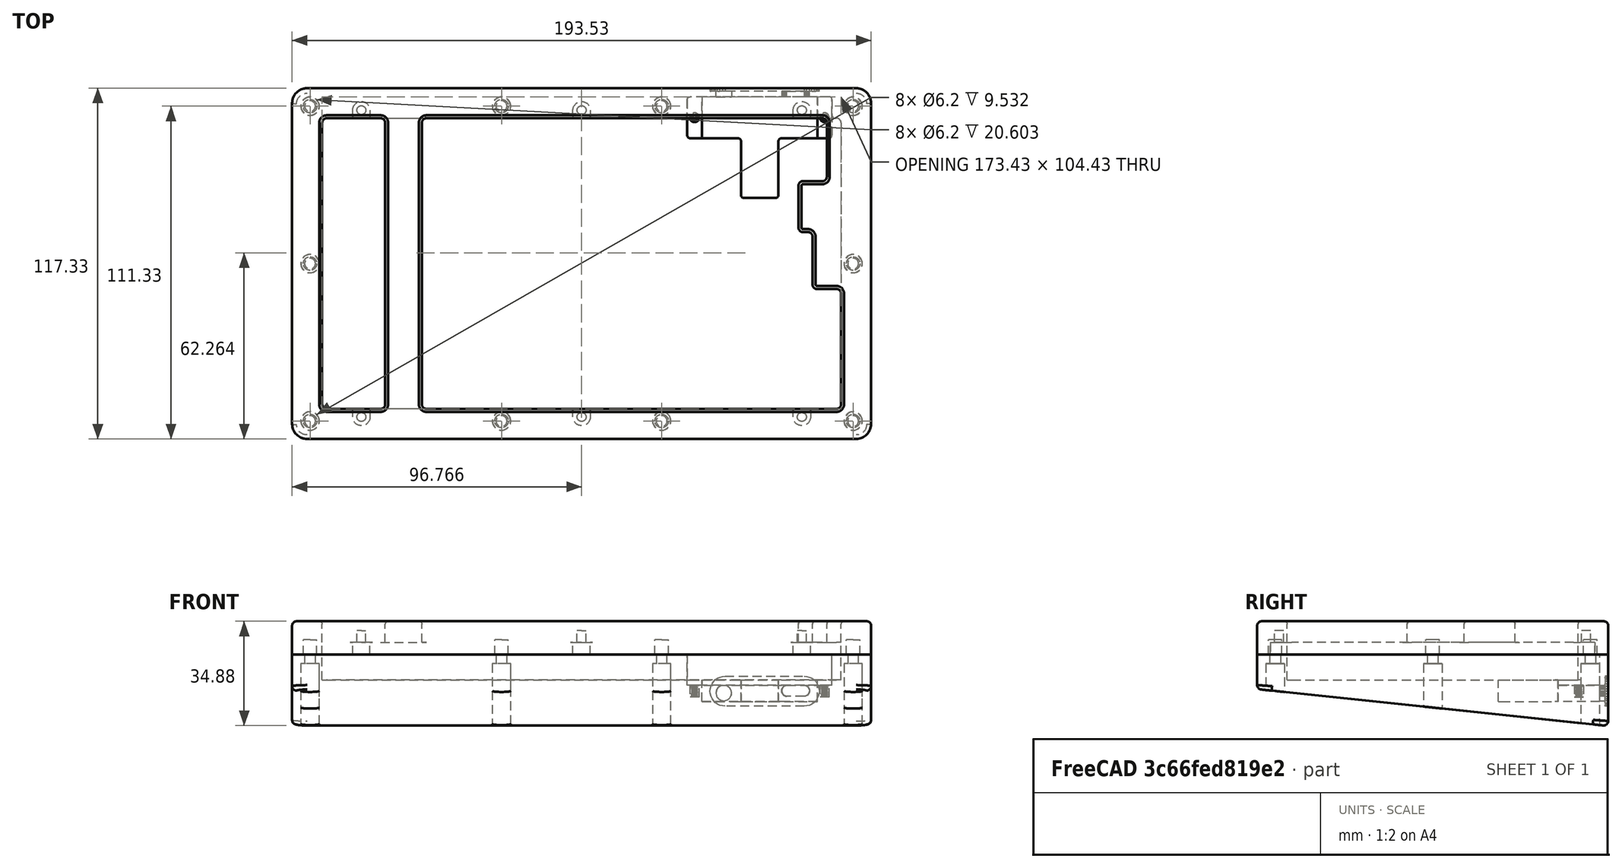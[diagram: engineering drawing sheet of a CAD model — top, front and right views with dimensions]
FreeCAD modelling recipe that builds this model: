
FCSTD DOCUMENT  (FreeCAD 0.21R33771 (Git))
Label: case_left
License: All rights reserved
LicenseURL: https://en.wikipedia.org/wiki/All_rights_reserved
objects: Part::Cylinder×44, Part::MultiFuse×41, Part::Feature×31, Part::Cut×19, Part::Fillet×18, Part::Extrusion×10, Part::Box×7, Part::FeaturePython×2
note: 172 computed .brp shape members not serialized (recipe doc carries the construction recipe); baked Part::Feature solids carry a one-line shape summary decoded from their .brp

FEATURE [Part::Feature] rect40_3 .. rect40_012  x10 (patterned run collapsed; names and placements below)
  shape: bbox 4.5 x 4.5 x 2e-07 mm, 0 faces, 0 solids (baked)
FEATURE [Part::Feature] rect40_013
  shape: bbox 173.4 x 108.4 x 2e-07 mm, 0 faces, 0 solids (baked)
FEATURE [Part::Box] Box  label="立方体"
  AttacherType = Attacher::AttachEngine3D
  Height = 11.2
  Length = 193.53
  Placement = pos=(0,-117.33,0) rot=(0,0,1;0rad)
  Width = 117.33
FEATURE [Part::MultiFuse] Fusion
  Shapes = -> [rect40_012,rect40_004,rect40_005,rect40_006,rect40_007,rect40_008,rect40_009,rect40_010,rect40_011,rect40_3]
FEATURE [Part::Extrusion] Extrude
  Base = -> Fusion
  Dir = (0,0,1)
  DirMode = 0
  FaceMakerClass = Part::FaceMakerBullseye
  LengthFwd = 5
  LengthRev = 0
  Solid = true
  Symmetric = false
FEATURE [Part::Extrusion] Extrude001
  Base = -> rect40_013
  Dir = (0,0,1)
  DirMode = 0
  FaceMakerClass = Part::FaceMakerBullseye
  LengthFwd = 4.1
  LengthRev = 0
  Solid = true
  Symmetric = false
FEATURE [Part::Cut] Cut
  Base = -> Box
  Tool = -> Extrude
FEATURE [Part::Cut] Cut001
  Base = -> Cut
  Tool = -> Extrude001
FEATURE [Part::Box] Box001  label="立方体001"
  AttacherType = Attacher::AttachEngine3D
  Height = 30
  Length = 193.53
  Placement = pos=(0,-117.33,-20) rot=(0,0,1;0rad)
  Width = 117.33
FEATURE [Part::Feature] path6845_6_2_7_83 .. path6845_6_2_7_088  x6 (patterned run collapsed; names and placements below)
  shape: bbox 3 x 3 x 2e-07 mm, 0 faces, 0 solids (baked)
FEATURE [Part::MultiFuse] Fusion001
  Shapes = -> [path6845_6_2_7_088,path6845_6_2_7_83,path6845_6_2_7_084,path6845_6_2_7_085,path6845_6_2_7_086,path6845_6_2_7_087]
FEATURE [Part::Extrusion] Extrude002
  Base = -> Fusion001
  Dir = (0,0,1)
  DirMode = 0
  FaceMakerClass = Part::FaceMakerBullseye
  LengthFwd = 4
  LengthRev = 0
  Placement = pos=(0,0,4.1) rot=(0,0,1;0rad)
  Solid = true
  Symmetric = false
FEATURE [Part::Cut] Cut002
  Base = -> Cut001
  Tool = -> Extrude002
FEATURE [Part::Feature] path44_5_0
  shape: bbox 140.1 x 97.23 x 2e-07 mm, 0 faces, 0 solids (baked)
FEATURE [Part::Feature] path44_5_001
  shape: bbox 21.05 x 97.23 x 2e-07 mm, 0 faces, 0 solids (baked)
FEATURE [Part::MultiFuse] Fusion002
  Shapes = -> [path44_5_0,path44_5_001]
FEATURE [Part::Extrusion] Extrude003
  Base = -> Fusion002
  Dir = (0,0,1)
  DirMode = 0
  FaceMakerClass = Part::FaceMakerBullseye
  LengthFwd = 7.1
  LengthRev = 0
  Placement = pos=(0,0,4.1) rot=(0,0,1;0rad)
  Solid = true
  Symmetric = false
FEATURE [Part::Fillet] Fillet
  Base = -> Cut002
  Edges = 12 edges r=0.8: [Edge135,Edge144,Edge146,Edge154,Edge156,Edge164,Edge170,Edge178,Edge180,Edge188,Edge190,Edge198]
FEATURE [Part::Fillet] Fillet001
  Base = -> Fillet
  Edges = 4 edges r=1.5: [Edge93,Edge97,Edge174,Edge178]
FEATURE [Part::Fillet] Fillet002
  Base = -> Extrude003
  Edges = 14 edges r=1.5: [Edge1,Edge2,Edge5,Edge8,Edge11,Edge14,Edge17,Edge20,Edge23,Edge26,Edge31,Edge32,Edge35,Edge38]
FEATURE [Part::Fillet] Fillet003
  Base = -> Fillet001
  Edges = 4 edges r=5: [Edge195,Edge197,Edge198,Edge201]
FEATURE [Part::Cut] Cut003
  Base = -> Fillet003
  Tool = -> Fillet002
FEATURE [Part::Box] Box002  label="立方体002"
  AttacherType = Attacher::AttachEngine3D
  Height = 100
  Length = 193.53
  Placement = pos=(0,-129.33,-100.8) rot=(-1,0,0;0.10472rad)
  Width = 150
FEATURE [Part::Cut] Cut004
  Base = -> Box001
  Tool = -> Box002
FEATURE [Part::Fillet] Fillet005
  Base = -> Cut004
  Edges = 4 edges r=5: [Edge1,Edge3,Edge5,Edge10]
FEATURE [Part::Fillet] Fillet006
  Base = -> Fillet005
  Edges = 8 edges r=1.5: [Edge3,Edge12,Edge14,Edge16,Edge17,Edge18,Edge19,Edge20]
FEATURE [Part::Fillet] Fillet007
  Base = -> Cut003
  Edges = 8 edges r=1.5: [Edge99,Edge103,Edge104,Edge107,Edge108,Edge111,Edge113,Edge114]
FEATURE [Part::Fillet] Fillet008  label="top_left"
  Base = -> Fillet007
  Edges = 28 edges r=1: [Edge119,Edge120,Edge121,Edge122,Edge123,Edge124,Edge125,Edge126,Edge127,Edge128,Edge129,Edge130,Edge131,Edge132,Edge133,Edge134,Edge135,Edge136,Edge137,Edge138,Edge139,Edge140,Edge141,Edge142,Edge143,Edge144,Edge145,Edge146]
  Placement = pos=(0,0,10) rot=(0,0,1;0rad)
FEATURE [Part::Cylinder] Cylinder045  label="円柱045"
  Angle = 360
  AttacherType = Attacher::AttachEngine3D
  FirstAngle = 0
  Height = 30
  Placement = pos=(0,0,-32) rot=(0,0,1;0rad)
  Radius = 3.1
  SecondAngle = 0
FEATURE [Part::Cylinder] Cylinder046  label="円柱046"
  Angle = 360
  AttacherType = Attacher::AttachEngine3D
  FirstAngle = 0
  Height = 20
  Placement = pos=(0,0,-10) rot=(0,0,1;0rad)
  Radius = 1.8
  SecondAngle = 0
FEATURE [Part::MultiFuse] Fusion048
  Placement = pos=(6,-6,0) rot=(0,0,1;0rad)
  Shapes = -> [Cylinder046,Cylinder045]
FEATURE [Part::Cylinder] Cylinder047  label="円柱047"
  Angle = 360
  AttacherType = Attacher::AttachEngine3D
  FirstAngle = 0
  Height = 30
  Placement = pos=(0,0,-32) rot=(0,0,1;0rad)
  Radius = 3.1
  SecondAngle = 0
FEATURE [Part::Cylinder] Cylinder048  label="円柱048"
  Angle = 360
  AttacherType = Attacher::AttachEngine3D
  FirstAngle = 0
  Height = 20
  Placement = pos=(0,0,-10) rot=(0,0,1;0rad)
  Radius = 1.8
  SecondAngle = 0
FEATURE [Part::MultiFuse] Fusion049
  Placement = pos=(6,-58.67,0) rot=(0,0,1;0rad)
  Shapes = -> [Cylinder048,Cylinder047]
FEATURE [Part::Cylinder] Cylinder049  label="円柱049"
  Angle = 360
  AttacherType = Attacher::AttachEngine3D
  FirstAngle = 0
  Height = 30
  Placement = pos=(0,0,-32) rot=(0,0,1;0rad)
  Radius = 3.1
  SecondAngle = 0
FEATURE [Part::Cylinder] Cylinder050  label="円柱050"
  Angle = 360
  AttacherType = Attacher::AttachEngine3D
  FirstAngle = 0
  Height = 20
  Placement = pos=(0,0,-10) rot=(0,0,1;0rad)
  Radius = 1.8
  SecondAngle = 0
FEATURE [Part::MultiFuse] Fusion050
  Placement = pos=(6,-111.34,0) rot=(0,0,1;0rad)
  Shapes = -> [Cylinder050,Cylinder049]
FEATURE [Part::MultiFuse] Fusion051
  Shapes = -> [Fusion050,Fusion049,Fusion048]
FEATURE [Part::Cylinder] Cylinder051  label="円柱051"
  Angle = 360
  AttacherType = Attacher::AttachEngine3D
  FirstAngle = 0
  Height = 30
  Placement = pos=(0,0,-32) rot=(0,0,1;0rad)
  Radius = 3.1
  SecondAngle = 0
FEATURE [Part::Cylinder] Cylinder052  label="円柱052"
  Angle = 360
  AttacherType = Attacher::AttachEngine3D
  FirstAngle = 0
  Height = 20
  Placement = pos=(0,0,-10) rot=(0,0,1;0rad)
  Radius = 1.8
  SecondAngle = 0
FEATURE [Part::Cylinder] Cylinder055  label="円柱055"
  Angle = 360
  AttacherType = Attacher::AttachEngine3D
  FirstAngle = 0
  Height = 30
  Placement = pos=(0,0,-32) rot=(0,0,1;0rad)
  Radius = 3.1
  SecondAngle = 0
FEATURE [Part::Cylinder] Cylinder056  label="円柱056"
  Angle = 360
  AttacherType = Attacher::AttachEngine3D
  FirstAngle = 0
  Height = 20
  Placement = pos=(0,0,-10) rot=(0,0,1;0rad)
  Radius = 1.8
  SecondAngle = 0
FEATURE [Part::MultiFuse] Fusion052
  Placement = pos=(6,-6,0) rot=(0,0,1;0rad)
  Shapes = -> [Cylinder052,Cylinder051]
FEATURE [Part::MultiFuse] Fusion054
  Placement = pos=(6,-111.34,0) rot=(0,0,1;0rad)
  Shapes = -> [Cylinder056,Cylinder055]
FEATURE [Part::MultiFuse] Fusion055
  Placement = pos=(64,0,0) rot=(0,0,1;0rad)
  Shapes = -> [Fusion054,Fusion052]
FEATURE [Part::Cylinder] Cylinder057  label="円柱057"
  Angle = 360
  AttacherType = Attacher::AttachEngine3D
  FirstAngle = 0
  Height = 30
  Placement = pos=(0,0,-32) rot=(0,0,1;0rad)
  Radius = 3.1
  SecondAngle = 0
FEATURE [Part::Cylinder] Cylinder058  label="円柱058"
  Angle = 360
  AttacherType = Attacher::AttachEngine3D
  FirstAngle = 0
  Height = 20
  Placement = pos=(0,0,-10) rot=(0,0,1;0rad)
  Radius = 1.8
  SecondAngle = 0
FEATURE [Part::Cylinder] Cylinder061  label="円柱061"
  Angle = 360
  AttacherType = Attacher::AttachEngine3D
  FirstAngle = 0
  Height = 30
  Placement = pos=(0,0,-32) rot=(0,0,1;0rad)
  Radius = 3.1
  SecondAngle = 0
FEATURE [Part::Cylinder] Cylinder062  label="円柱062"
  Angle = 360
  AttacherType = Attacher::AttachEngine3D
  FirstAngle = 0
  Height = 20
  Placement = pos=(0,0,-10) rot=(0,0,1;0rad)
  Radius = 1.8
  SecondAngle = 0
FEATURE [Part::MultiFuse] Fusion056
  Placement = pos=(6,-6,0) rot=(0,0,1;0rad)
  Shapes = -> [Cylinder058,Cylinder057]
FEATURE [Part::MultiFuse] Fusion058
  Placement = pos=(6,-111.34,0) rot=(0,0,1;0rad)
  Shapes = -> [Cylinder062,Cylinder061]
FEATURE [Part::MultiFuse] Fusion059
  Placement = pos=(117.53,0,0) rot=(0,0,1;0rad)
  Shapes = -> [Fusion058,Fusion056]
FEATURE [Part::Cylinder] Cylinder063  label="円柱063"
  Angle = 360
  AttacherType = Attacher::AttachEngine3D
  FirstAngle = 0
  Height = 30
  Placement = pos=(0,0,-32) rot=(0,0,1;0rad)
  Radius = 3.1
  SecondAngle = 0
FEATURE [Part::Cylinder] Cylinder064  label="円柱064"
  Angle = 360
  AttacherType = Attacher::AttachEngine3D
  FirstAngle = 0
  Height = 20
  Placement = pos=(0,0,-10) rot=(0,0,1;0rad)
  Radius = 1.8
  SecondAngle = 0
FEATURE [Part::Cylinder] Cylinder065  label="円柱065"
  Angle = 360
  AttacherType = Attacher::AttachEngine3D
  FirstAngle = 0
  Height = 30
  Placement = pos=(0,0,-32) rot=(0,0,1;0rad)
  Radius = 3.1
  SecondAngle = 0
FEATURE [Part::Cylinder] Cylinder066  label="円柱066"
  Angle = 360
  AttacherType = Attacher::AttachEngine3D
  FirstAngle = 0
  Height = 20
  Placement = pos=(0,0,-10) rot=(0,0,1;0rad)
  Radius = 1.8
  SecondAngle = 0
FEATURE [Part::Cylinder] Cylinder067  label="円柱067"
  Angle = 360
  AttacherType = Attacher::AttachEngine3D
  FirstAngle = 0
  Height = 30
  Placement = pos=(0,0,-32) rot=(0,0,1;0rad)
  Radius = 3.1
  SecondAngle = 0
FEATURE [Part::Cylinder] Cylinder068  label="円柱068"
  Angle = 360
  AttacherType = Attacher::AttachEngine3D
  FirstAngle = 0
  Height = 20
  Placement = pos=(0,0,-10) rot=(0,0,1;0rad)
  Radius = 1.8
  SecondAngle = 0
FEATURE [Part::MultiFuse] Fusion060
  Placement = pos=(6,-6,0) rot=(0,0,1;0rad)
  Shapes = -> [Cylinder064,Cylinder063]
FEATURE [Part::MultiFuse] Fusion061
  Placement = pos=(6,-58.67,0) rot=(0,0,1;0rad)
  Shapes = -> [Cylinder066,Cylinder065]
FEATURE [Part::MultiFuse] Fusion062
  Placement = pos=(6,-111.34,0) rot=(0,0,1;0rad)
  Shapes = -> [Cylinder068,Cylinder067]
FEATURE [Part::MultiFuse] Fusion063
  Placement = pos=(181.53,0,0) rot=(0,0,1;0rad)
  Shapes = -> [Fusion062,Fusion061,Fusion060]
FEATURE [Part::MultiFuse] Fusion064
  Placement = pos=(0,0,9) rot=(0,0,1;0rad)
  Shapes = -> [Fusion063,Fusion059,Fusion055,Fusion051]
FEATURE [Part::Cut] Cut005
  Base = -> Fillet006
  Tool = -> Fusion064
FEATURE [Part::Feature] path6845_6_2_7_83_9
  shape: bbox 173.4 x 97.23 x 2e-07 mm, 0 faces, 0 solids (baked)
FEATURE [Part::Extrusion] Extrude004
  Base = -> path6845_6_2_7_83_9
  Dir = (0,0,1)
  DirMode = 0
  FaceMakerClass = Part::FaceMakerBullseye
  LengthFwd = 8.5
  LengthRev = 0
  Placement = pos=(0,0,1.5) rot=(0,0,1;0rad)
  Solid = true
  Symmetric = false
FEATURE [Part::Fillet] Fillet009
  Base = -> Extrude004
  Edges = 4 edges r=1.5: [Edge1,Edge2,Edge5,Edge8]
FEATURE [Part::Cut] Cut006
  Base = -> Cut005
  Tool = -> Fillet009
FEATURE [Part::Cylinder] Cylinder  label="円柱"
  Angle = 360
  AttacherType = Attacher::AttachEngine3D
  FirstAngle = 0
  Height = 4
  Placement = pos=(15.57,-9.8,-4.2) rot=(0,0,1;0rad)
  Radius = 1.55
  SecondAngle = 0
FEATURE [Part::Cylinder] Cylinder069  label="円柱069"
  Angle = 360
  AttacherType = Attacher::AttachEngine3D
  FirstAngle = 0
  Height = 4
  Placement = pos=(59.03,-9.8,-4.2) rot=(0,0,1;0rad)
  Radius = 1.55
  SecondAngle = 0
FEATURE [Part::Cylinder] Cylinder070  label="trrs"
  Angle = 360
  AttacherType = Attacher::AttachEngine3D
  FirstAngle = 0
  Height = 10
  Placement = pos=(144.28,5,-2.81) rot=(1,0,0;1.5708rad)
  Radius = 2.6
  SecondAngle = 0
FEATURE [Part::MultiFuse] Fusion065
  Placement = pos=(118.94,0,0) rot=(0,0,1;0rad)
  Shapes = -> [Cylinder,Cylinder069]
FEATURE [Part::Feature] hull006
  Placement = pos=(0,4.8,0) rot=(0,0,1;0rad)
  shape: bbox 13.02 x 10 x 7.518 mm, 128 faces (baked)
FEATURE [Part::Feature] hull007
  shape: bbox 9.26 x 10 x 3.733 mm, 28 faces (baked)
FEATURE [Part::MultiFuse] Fusion067  label="usb-hole001"
  Placement = pos=(-147.56,-1.85,-4.55) rot=(0,0,1;0rad)
  Shapes = -> [hull006,hull007]
FEATURE [Part::Box] Box003  label="立方体003"
  AttacherType = Attacher::AttachEngine3D
  Height = 7.2
  Length = 12.5
  Placement = pos=(31.05,-36.75,-5.7) rot=(0,0,1;0rad)
  Width = 20
FEATURE [Part::Feature] rect3_6_21_5
  Placement = pos=(0,0,-0.2) rot=(0,0,1;0rad)
  shape: bbox 38.6 x 13.9 x 2e-07 mm, 0 faces, 0 solids (baked)
FEATURE [Part::Extrusion] Extrude007
  Base = -> rect3_6_21_5
  Dir = (0,0,1)
  DirMode = 0
  FaceMakerClass = Part::FaceMakerBullseye
  LengthFwd = 22.2
  LengthRev = 0
  Placement = pos=(0,0,-5.5) rot=(0,0,1;0rad)
  Solid = true
  Symmetric = false
FEATURE [Part::MultiFuse] Fusion066
  Placement = pos=(119,0,0) rot=(0,0,1;0rad)
  Shapes = -> [Extrude007,Box003]
FEATURE [Part::Cut] Cut007
  Base = -> Cut006
  Tool = -> Fusion066
FEATURE [Part::Fillet] Fillet010
  Base = -> Cut007
  Edges = 4 edges r=1: [Edge151,Edge152,Edge154,Edge156]
FEATURE [Part::Feature] rect3_6
  Placement = pos=(0,0,-0.2) rot=(0,0,1;0rad)
  shape: bbox 48.4 x 13.9 x 2e-07 mm, 0 faces, 0 solids (baked)
FEATURE [Part::Extrusion] Extrude008
  Base = -> rect3_6
  Dir = (0,0,1)
  DirMode = 0
  FaceMakerClass = Part::FaceMakerBullseye
  LengthFwd = 16.7
  LengthRev = 0
  Solid = true
  Symmetric = false
FEATURE [Part::Fillet] Fillet011
  Base = -> Extrude008
  Edges = 4 edges r=1: [Edge1,Edge2,Edge5,Edge8]
FEATURE [Part::Cut] Cut008
  Base = -> Fillet010
  Tool = -> Fillet011
FEATURE [Part::Fillet] Fillet012
  Base = -> Cut008
  Edges = 2 edges r=1: [Edge53,Edge72]
FEATURE [Part::Cut] Cut009
  Base = -> Fillet012
  Tool = -> Fusion065
FEATURE [Part::Cut] Cut010
  Base = -> Cut009
  Tool = -> Fusion067
FEATURE [Part::Cut] Cut011
  Base = -> Cut010
  Tool = -> Cylinder070
FEATURE [Part::Feature] hull
  Placement = pos=(121.9,0,0) rot=(0,0,1;0rad)
  shape: bbox 36.5 x 3 x 10 mm, 40 faces (baked)
FEATURE [Part::Cut] Cut012  label="bottom_left"
  Base = -> Cut011
  Tool = -> hull
FEATURE [Part::Box] Box004  label="立方体004"
  AttacherType = Attacher::AttachEngine3D
  Height = 30
  Length = 193.53
  Placement = pos=(0,-117.33,-20) rot=(0,0,1;0rad)
  Width = 117.33
FEATURE [Part::Box] Box005  label="立方体005"
  AttacherType = Attacher::AttachEngine3D
  Height = 100
  Length = 193.53
  Placement = pos=(0,-129.33,-100.8) rot=(-1,0,0;0.10472rad)
  Width = 150
FEATURE [Part::Box] Box006  label="立方体006"
  AttacherType = Attacher::AttachEngine3D
  Height = 7.2
  Length = 12.5
  Placement = pos=(31.05,-36.75,-5.7) rot=(0,0,1;0rad)
  Width = 20
FEATURE [Part::Cut] Cut013
  Base = -> Box004
  Tool = -> Box005
FEATURE [Part::Cylinder] Cylinder072  label="円柱071"
  Angle = 360
  AttacherType = Attacher::AttachEngine3D
  FirstAngle = 0
  Height = 30
  Placement = pos=(0,0,-32) rot=(0,0,1;0rad)
  Radius = 3.1
  SecondAngle = 0
FEATURE [Part::Cylinder] Cylinder073  label="円柱072"
  Angle = 360
  AttacherType = Attacher::AttachEngine3D
  FirstAngle = 0
  Height = 20
  Placement = pos=(0,0,-10) rot=(0,0,1;0rad)
  Radius = 1.8
  SecondAngle = 0
FEATURE [Part::Cylinder] Cylinder074  label="円柱073"
  Angle = 360
  AttacherType = Attacher::AttachEngine3D
  FirstAngle = 0
  Height = 30
  Placement = pos=(0,0,-32) rot=(0,0,1;0rad)
  Radius = 3.1
  SecondAngle = 0
FEATURE [Part::Cylinder] Cylinder075  label="円柱074"
  Angle = 360
  AttacherType = Attacher::AttachEngine3D
  FirstAngle = 0
  Height = 20
  Placement = pos=(0,0,-10) rot=(0,0,1;0rad)
  Radius = 1.8
  SecondAngle = 0
FEATURE [Part::Cylinder] Cylinder076  label="円柱075"
  Angle = 360
  AttacherType = Attacher::AttachEngine3D
  FirstAngle = 0
  Height = 30
  Placement = pos=(0,0,-32) rot=(0,0,1;0rad)
  Radius = 3.1
  SecondAngle = 0
FEATURE [Part::Cylinder] Cylinder077  label="円柱076"
  Angle = 360
  AttacherType = Attacher::AttachEngine3D
  FirstAngle = 0
  Height = 20
  Placement = pos=(0,0,-10) rot=(0,0,1;0rad)
  Radius = 1.8
  SecondAngle = 0
FEATURE [Part::Cylinder] Cylinder078  label="円柱077"
  Angle = 360
  AttacherType = Attacher::AttachEngine3D
  FirstAngle = 0
  Height = 30
  Placement = pos=(0,0,-32) rot=(0,0,1;0rad)
  Radius = 3.1
  SecondAngle = 0
FEATURE [Part::Cylinder] Cylinder079  label="円柱078"
  Angle = 360
  AttacherType = Attacher::AttachEngine3D
  FirstAngle = 0
  Height = 20
  Placement = pos=(0,0,-10) rot=(0,0,1;0rad)
  Radius = 1.8
  SecondAngle = 0
FEATURE [Part::Cylinder] Cylinder080  label="円柱079"
  Angle = 360
  AttacherType = Attacher::AttachEngine3D
  FirstAngle = 0
  Height = 30
  Placement = pos=(0,0,-32) rot=(0,0,1;0rad)
  Radius = 3.1
  SecondAngle = 0
FEATURE [Part::Cylinder] Cylinder081  label="円柱080"
  Angle = 360
  AttacherType = Attacher::AttachEngine3D
  FirstAngle = 0
  Height = 20
  Placement = pos=(0,0,-10) rot=(0,0,1;0rad)
  Radius = 1.8
  SecondAngle = 0
FEATURE [Part::Cylinder] Cylinder082  label="円柱081"
  Angle = 360
  AttacherType = Attacher::AttachEngine3D
  FirstAngle = 0
  Height = 30
  Placement = pos=(0,0,-32) rot=(0,0,1;0rad)
  Radius = 3.1
  SecondAngle = 0
FEATURE [Part::Cylinder] Cylinder083  label="円柱082"
  Angle = 360
  AttacherType = Attacher::AttachEngine3D
  FirstAngle = 0
  Height = 20
  Placement = pos=(0,0,-10) rot=(0,0,1;0rad)
  Radius = 1.8
  SecondAngle = 0
FEATURE [Part::Cylinder] Cylinder084  label="円柱083"
  Angle = 360
  AttacherType = Attacher::AttachEngine3D
  FirstAngle = 0
  Height = 30
  Placement = pos=(0,0,-32) rot=(0,0,1;0rad)
  Radius = 3.1
  SecondAngle = 0
FEATURE [Part::Cylinder] Cylinder085  label="円柱084"
  Angle = 360
  AttacherType = Attacher::AttachEngine3D
  FirstAngle = 0
  Height = 20
  Placement = pos=(0,0,-10) rot=(0,0,1;0rad)
  Radius = 1.8
  SecondAngle = 0
FEATURE [Part::Cylinder] Cylinder086  label="円柱085"
  Angle = 360
  AttacherType = Attacher::AttachEngine3D
  FirstAngle = 0
  Height = 30
  Placement = pos=(0,0,-32) rot=(0,0,1;0rad)
  Radius = 3.1
  SecondAngle = 0
FEATURE [Part::Cylinder] Cylinder087  label="円柱086"
  Angle = 360
  AttacherType = Attacher::AttachEngine3D
  FirstAngle = 0
  Height = 20
  Placement = pos=(0,0,-10) rot=(0,0,1;0rad)
  Radius = 1.8
  SecondAngle = 0
FEATURE [Part::Cylinder] Cylinder088  label="円柱087"
  Angle = 360
  AttacherType = Attacher::AttachEngine3D
  FirstAngle = 0
  Height = 30
  Placement = pos=(0,0,-32) rot=(0,0,1;0rad)
  Radius = 3.1
  SecondAngle = 0
FEATURE [Part::Cylinder] Cylinder089  label="円柱088"
  Angle = 360
  AttacherType = Attacher::AttachEngine3D
  FirstAngle = 0
  Height = 20
  Placement = pos=(0,0,-10) rot=(0,0,1;0rad)
  Radius = 1.8
  SecondAngle = 0
FEATURE [Part::Cylinder] Cylinder090  label="円柱089"
  Angle = 360
  AttacherType = Attacher::AttachEngine3D
  FirstAngle = 0
  Height = 30
  Placement = pos=(0,0,-32) rot=(0,0,1;0rad)
  Radius = 3.1
  SecondAngle = 0
FEATURE [Part::Cylinder] Cylinder091  label="円柱090"
  Angle = 360
  AttacherType = Attacher::AttachEngine3D
  FirstAngle = 0
  Height = 20
  Placement = pos=(0,0,-10) rot=(0,0,1;0rad)
  Radius = 1.8
  SecondAngle = 0
FEATURE [Part::Cylinder] Cylinder093  label="trrs001"
  Angle = 360
  AttacherType = Attacher::AttachEngine3D
  FirstAngle = 0
  Height = 10
  Placement = pos=(144.28,5,-2.81) rot=(1,0,0;1.5708rad)
  Radius = 2.6
  SecondAngle = 0
FEATURE [Part::Fillet] Fillet013
  Base = -> Cut013
  Edges = 4 edges r=5: [Edge1,Edge3,Edge5,Edge10]
FEATURE [Part::Fillet] Fillet014
  Base = -> Fillet013
  Edges = 8 edges r=1.5: [Edge3,Edge12,Edge14,Edge16,Edge17,Edge18,Edge19,Edge20]
FEATURE [Part::MultiFuse] Fusion068
  Placement = pos=(6,-6,0) rot=(0,0,1;0rad)
  Shapes = -> [Cylinder073,Cylinder072]
FEATURE [Part::MultiFuse] Fusion069
  Placement = pos=(6,-58.67,0) rot=(0,0,1;0rad)
  Shapes = -> [Cylinder075,Cylinder074]
FEATURE [Part::MultiFuse] Fusion070
  Placement = pos=(6,-111.34,0) rot=(0,0,1;0rad)
  Shapes = -> [Cylinder077,Cylinder076]
FEATURE [Part::MultiFuse] Fusion071
  Shapes = -> [Fusion070,Fusion069,Fusion068]
FEATURE [Part::MultiFuse] Fusion072
  Placement = pos=(6,-6,0) rot=(0,0,1;0rad)
  Shapes = -> [Cylinder079,Cylinder078]
FEATURE [Part::MultiFuse] Fusion073
  Placement = pos=(6,-111.34,0) rot=(0,0,1;0rad)
  Shapes = -> [Cylinder081,Cylinder080]
FEATURE [Part::MultiFuse] Fusion074
  Placement = pos=(64,0,0) rot=(0,0,1;0rad)
  Shapes = -> [Fusion073,Fusion072]
FEATURE [Part::MultiFuse] Fusion075
  Placement = pos=(6,-6,0) rot=(0,0,1;0rad)
  Shapes = -> [Cylinder083,Cylinder082]
FEATURE [Part::MultiFuse] Fusion076
  Placement = pos=(6,-111.34,0) rot=(0,0,1;0rad)
  Shapes = -> [Cylinder085,Cylinder084]
FEATURE [Part::MultiFuse] Fusion077
  Placement = pos=(117.53,0,0) rot=(0,0,1;0rad)
  Shapes = -> [Fusion076,Fusion075]
FEATURE [Part::MultiFuse] Fusion078
  Placement = pos=(6,-6,0) rot=(0,0,1;0rad)
  Shapes = -> [Cylinder087,Cylinder086]
FEATURE [Part::MultiFuse] Fusion079
  Placement = pos=(6,-58.67,0) rot=(0,0,1;0rad)
  Shapes = -> [Cylinder089,Cylinder088]
FEATURE [Part::MultiFuse] Fusion080
  Placement = pos=(6,-111.34,0) rot=(0,0,1;0rad)
  Shapes = -> [Cylinder091,Cylinder090]
FEATURE [Part::MultiFuse] Fusion081
  Placement = pos=(181.53,0,0) rot=(0,0,1;0rad)
  Shapes = -> [Fusion080,Fusion079,Fusion078]
FEATURE [Part::MultiFuse] Fusion082
  Placement = pos=(0,0,9) rot=(0,0,1;0rad)
  Shapes = -> [Fusion081,Fusion077,Fusion074,Fusion071]
FEATURE [Part::Cut] Cut014
  Base = -> Fillet014
  Tool = -> Fusion082
FEATURE [Part::Feature] hull008
  Placement = pos=(121.9,0,0) rot=(0,0,1;0rad)
  shape: bbox 36.5 x 3 x 10 mm, 40 faces (baked)
FEATURE [Part::Feature] hull009
  Placement = pos=(0,4.8,0) rot=(0,0,1;0rad)
  shape: bbox 13.02 x 10 x 7.518 mm, 128 faces (baked)
FEATURE [Part::Feature] hull010
  shape: bbox 9.26 x 10 x 3.733 mm, 28 faces (baked)
FEATURE [Part::MultiFuse] Fusion085  label="usb-hole002"
  Placement = pos=(-147.56,-1.85,-4.55) rot=(0,0,1;0rad)
  Shapes = -> [hull009,hull010]
FEATURE [Part::Feature] path6845_6_2_7_83_010
  shape: bbox 173.4 x 97.23 x 2e-07 mm, 0 faces, 0 solids (baked)
FEATURE [Part::Extrusion] Extrude009
  Base = -> path6845_6_2_7_83_010
  Dir = (0,0,1)
  DirMode = 0
  FaceMakerClass = Part::FaceMakerBullseye
  LengthFwd = 8.5
  LengthRev = 0
  Placement = pos=(0,0,1.5) rot=(0,0,1;0rad)
  Solid = true
  Symmetric = false
FEATURE [Part::Fillet] Fillet015
  Base = -> Extrude009
  Edges = 4 edges r=1.5: [Edge1,Edge2,Edge5,Edge8]
FEATURE [Part::Cut] Cut015
  Base = -> Cut014
  Tool = -> Fillet015
FEATURE [Part::Feature] rect3_007
  Placement = pos=(0,0,-0.2) rot=(0,0,1;0rad)
  shape: bbox 48.4 x 13.9 x 2e-07 mm, 0 faces, 0 solids (baked)
FEATURE [Part::Extrusion] Extrude011
  Base = -> rect3_007
  Dir = (0,0,1)
  DirMode = 0
  FaceMakerClass = Part::FaceMakerBullseye
  LengthFwd = 16.7
  LengthRev = 0
  Solid = true
  Symmetric = false
FEATURE [Part::Fillet] Fillet017
  Base = -> Extrude011
  Edges = 4 edges r=1: [Edge1,Edge2,Edge5,Edge8]
FEATURE [Part::Feature] rect3_6_21_006
  Placement = pos=(0,0,-0.2) rot=(0,0,1;0rad)
  shape: bbox 38.6 x 13.9 x 2e-07 mm, 0 faces, 0 solids (baked)
FEATURE [Part::Extrusion] Extrude010
  Base = -> rect3_6_21_006
  Dir = (0,0,1)
  DirMode = 0
  FaceMakerClass = Part::FaceMakerBullseye
  LengthFwd = 22.2
  LengthRev = 0
  Placement = pos=(0,0,-5.5) rot=(0,0,1;0rad)
  Solid = true
  Symmetric = false
FEATURE [Part::MultiFuse] Fusion084
  Placement = pos=(119,0,0) rot=(0,0,1;0rad)
  Shapes = -> [Extrude010,Box006]
FEATURE [Part::Cut] Cut016
  Base = -> Cut015
  Tool = -> Fusion084
FEATURE [Part::Fillet] Fillet016
  Base = -> Cut016
  Edges = 4 edges r=1: [Edge151,Edge152,Edge154,Edge156]
FEATURE [Part::Cut] Cut017
  Base = -> Fillet016
  Tool = -> Fillet017
FEATURE [Part::Fillet] Fillet018
  Base = -> Cut017
  Edges = 2 edges r=1: [Edge53,Edge72]
FEATURE [Part::MultiFuse] Fusion086
  Shapes = -> [Cylinder093,Fusion085]
FEATURE [Part::FeaturePython] ThreadedRod001  label="M2x5-ThreadedRod"  # Fasteners workbench fastener (typed FeaturePython)
  Placement = pos=(59.03,-9.8,0.8) rot=(0,0,1;0rad)
  diameter = 2
  diameterCustom = 6
  invert = false
  leftHanded = false
  length = 5
  matchOuter = false
  offset = 0
  pitchCustom = 1
  thread = true
  type = 4
FEATURE [Part::FeaturePython] ThreadedRod  label="M2x5-ThreadedRod001"  # Fasteners workbench fastener (typed FeaturePython)
  Placement = pos=(15.57,-9.8,0.8) rot=(0,0,1;0rad)
  diameter = 2
  diameterCustom = 6
  invert = false
  leftHanded = false
  length = 5
  matchOuter = false
  offset = 0
  pitchCustom = 1
  thread = true
  type = 4
FEATURE [Part::MultiFuse] Fusion087
  Placement = pos=(118.95,0,0) rot=(0,0,1;0rad)
  Shapes = -> [ThreadedRod,ThreadedRod001]
FEATURE [Part::MultiFuse] Fusion088
  Shapes = -> [Fusion086,Fusion087,hull008]
FEATURE [Part::Cut] Cut018  label="bottom_left_resin"
  Base = -> Fillet018
  Tool = -> Fusion088
